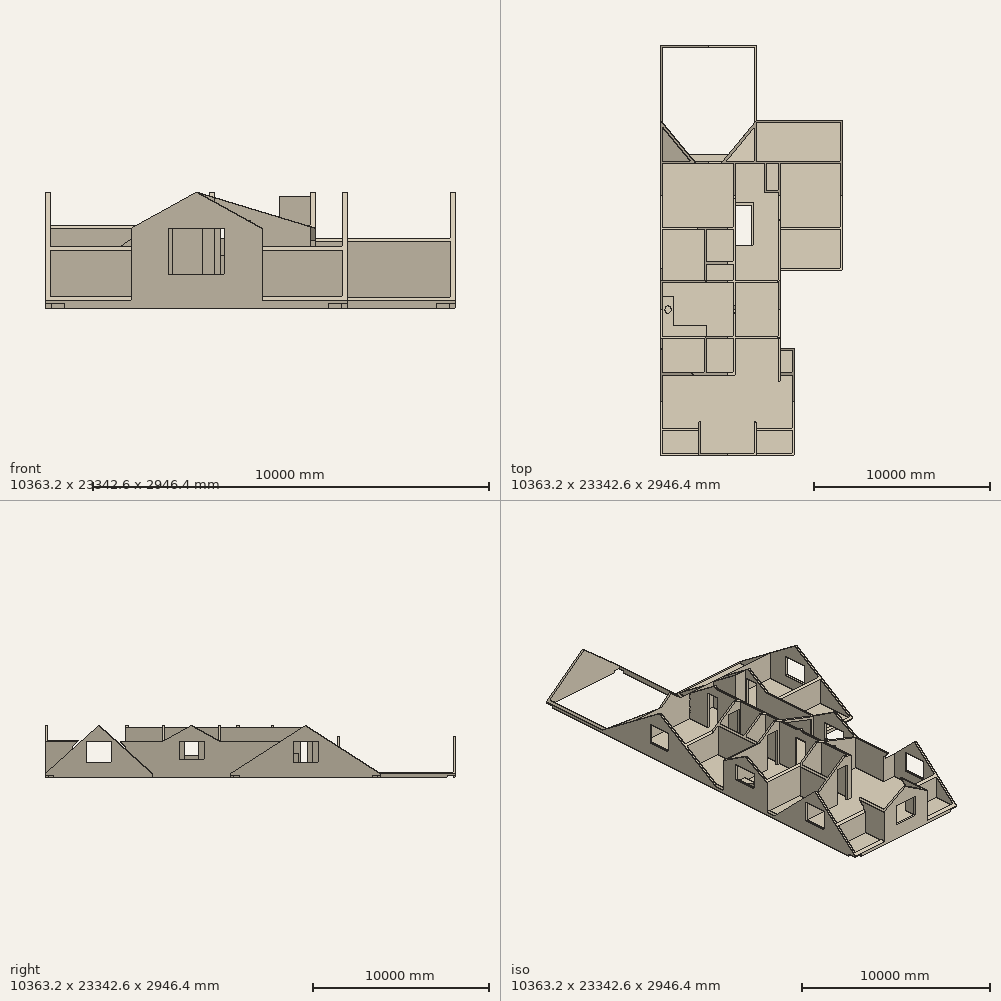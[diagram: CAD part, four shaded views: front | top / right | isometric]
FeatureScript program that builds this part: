
annotation { "Feature Type Name" : "Feature", "Feature Type Description" : "" }
export const myFeature = defineFeature(function(context is Context, id is Id, definition is map)
    precondition{}
    {
        {
            var Q0;
            Q0=qCreatedBy(makeId("Top.planeOp"),FACE);
            cPlane(context, id + "F0", {"entities" : qUnion([Q0]), "cplaneType" : CPlaneType.OFFSET, "offset" : 2946.4 * mm, "width" : 152.4 * mm, "height" : 152.4 * mm});
        }
        {
            var Q0;
            Q0=qCreatedBy(makeId("Top.planeOp"),FACE);
            var sketch = newSketch(context, id + "F1", { "sketchPlane" : qUnion([Q0])});
            skLineSegment(sketch, "E0", {"start": v(0, 0) * mm, "end": v(7645.4, 0) * mm});
            skLineSegment(sketch, "E1", {"start": v(7645.4, 0) * mm, "end": v(7645.4, 6096) * mm});
            skLineSegment(sketch, "E2", {"start": v(7645.4, 6096) * mm, "end": v(6832.6, 6096) * mm});
            skLineSegment(sketch, "E3", {"start": v(6832.6, 6096) * mm, "end": v(6832.6, 10541) * mm});
            skLineSegment(sketch, "E4", {"start": v(6832.6, 10541) * mm, "end": v(10363.2, 10541) * mm});
            skLineSegment(sketch, "E5", {"start": v(10363.2, 10541) * mm, "end": v(10363.2, 19075.4) * mm});
            skLineSegment(sketch, "E6", {"start": v(10363.2, 19075.4) * mm, "end": v(5486.4, 19075.4) * mm});
            skLineSegment(sketch, "E7", {"start": v(5486.4, 19075.4) * mm, "end": v(5486.4, 23342.6) * mm});
            skLineSegment(sketch, "E8", {"start": v(5486.4, 23342.6) * mm, "end": v(0, 23342.6) * mm});
            skLineSegment(sketch, "E9", {"start": v(0, 23342.6) * mm, "end": v(0, 0) * mm});
            skSolve(sketch);
        }
        {
            var Q0;
            Q0=qSketchRegion(id+"F1",true);
            extrude(context, id + "F2", {"entities" : qUnion([Q0]), "depth" : 2946.4 * mm});
        }
        {
            var Q0;
            Q0=makeQuery(id+"F2.opExtrude","SWEPT_FACE",FACE,{"disambiguationData":[OSD([sQuery(id+"F1.wireOp",EDGE,"E5")])]});
            var sketch = newSketch(context, id + "F3", { "sketchPlane" : qUnion([Q0])});
            skLineSegment(sketch, "E10", {"start": v(10541, 203.2) * mm, "end": v(19075.4, 203.2) * mm, "construction": true});
            skLineSegment(sketch, "E11", {"start": v(14808.2, 203.2) * mm, "end": v(14808.2, 2946.4) * mm, "construction": true});
            skLineSegment(sketch, "E12", {"start": v(10541, 203.2) * mm, "end": v(14808.2, 2946.4) * mm});
            skLineSegment(sketch, "E13", {"start": v(10541, 203.2) * mm, "end": v(10541, 2946.4) * mm});
            skLineSegment(sketch, "E14", {"start": v(10541, 2946.4) * mm, "end": v(19075.4, 2946.4) * mm});
            skLineSegment(sketch, "E15", {"start": v(19075.4, 2946.4) * mm, "end": v(19075.4, 203.2) * mm});
            skLineSegment(sketch, "E16", {"start": v(19075.4, 203.2) * mm, "end": v(14808.2, 2946.4) * mm});
            skLineSegment(sketch, "E17", {"start": v(6096, 203.2) * mm, "end": v(0, 203.2) * mm, "construction": true});
            skLineSegment(sketch, "E18", {"start": v(3048, 203.2) * mm, "end": v(3048, 2946.4) * mm, "construction": true});
            skLineSegment(sketch, "E19", {"start": v(3048, 2946.4) * mm, "end": v(0, 203.2) * mm});
            skLineSegment(sketch, "E20", {"start": v(0, 203.2) * mm, "end": v(0, 2946.4) * mm});
            skLineSegment(sketch, "E21", {"start": v(0, 2946.4) * mm, "end": v(6096, 2946.4) * mm});
            skLineSegment(sketch, "E22", {"start": v(6096, 2946.4) * mm, "end": v(6096, 203.2) * mm});
            skLineSegment(sketch, "E23", {"start": v(6096, 203.2) * mm, "end": v(3048, 2946.4) * mm});
            skSolve(sketch);
        }
        {
            var Q0;
            Q0=qSketchRegion(id+"F3",true);
            extrude(context, id + "F4", {"entities" : qUnion([Q0]), "operationType" : NewBodyOperationType.REMOVE, "endBound" : BoundingType.THROUGH_ALL, "oppositeDirection" : true, "depth" : 25.4 * mm});
        }
        {
            var Q0;
            Q0=makeQuery(id+"F2.opExtrude","SWEPT_FACE",FACE,{"disambiguationData":[OSD([sQuery(id+"F1.wireOp",EDGE,"E8")])]});
            var sketch = newSketch(context, id + "F5", { "sketchPlane" : qUnion([Q0])});
            skLineSegment(sketch, "E24", {"start": v(-5486.4, 203.2) * mm, "end": v(0, 203.2) * mm, "construction": true});
            skLineSegment(sketch, "E25", {"start": v(-2743.2, 203.2) * mm, "end": v(-2743.2, 2336.8) * mm, "construction": true});
            skLineSegment(sketch, "E26", {"start": v(-5486.4, 203.2) * mm, "end": v(-2743.2, 2336.8) * mm});
            skLineSegment(sketch, "E27", {"start": v(-2743.2, 2336.8) * mm, "end": v(0, 203.2) * mm});
            skLineSegment(sketch, "E28", {"start": v(-5486.4, 203.2) * mm, "end": v(-5486.4, 2946.4) * mm});
            skLineSegment(sketch, "E29", {"start": v(-5486.4, 2946.4) * mm, "end": v(0, 2946.4) * mm});
            skLineSegment(sketch, "E30", {"start": v(0, 2946.4) * mm, "end": v(0, 203.2) * mm});
            skSolve(sketch);
        }
        {
            var Q0;
            Q0=qSketchRegion(id+"F5",true);
            extrude(context, id + "F6", {"entities" : qUnion([Q0]), "operationType" : NewBodyOperationType.REMOVE, "oppositeDirection" : true, "depth" : 4267.2 * mm});
        }
        {
            var Q0;
            Q0=makeQuery(id+"F4.boolean.opBoolean","COPY",FACE,{"derivedFrom":makeQuery(id+"F4.opExtrude","SWEPT_FACE",FACE,{"disambiguationData":[OSD([sQuery(id+"F3.wireOp",EDGE,"E15")])]})});
            var sketch = newSketch(context, id + "F7", { "sketchPlane" : qUnion([Q0])});
            skLineSegment(sketch, "E31", {"start": v(0, 203.2) * mm, "end": v(2743.2, 2336.8) * mm});
            skLineSegment(sketch, "E32", {"start": v(2743.2, 2336.8) * mm, "end": v(5486.4, 203.2) * mm});
            skLineSegment(sketch, "E33", {"start": v(5486.4, 203.2) * mm, "end": v(0, 203.2) * mm});
            skSolve(sketch);
        }
        {
            var Q0;
            Q0=qSketchRegion(id+"F7",true);
            extrude(context, id + "F8", {"entities" : qUnion([Q0]), "operationType" : NewBodyOperationType.ADD, "endBound" : BoundingType.UP_TO_NEXT, "depth" : 25.4 * mm});
        }
        {
            var Q0;
            Q0=makeQuery(id+"F4.boolean.opBoolean","COPY",FACE,{"derivedFrom":makeQuery(id+"F4.opExtrude","SWEPT_FACE",FACE,{"disambiguationData":[OSD([sQuery(id+"F3.wireOp",EDGE,"E22")])]})});
            var sketch = newSketch(context, id + "F9", { "sketchPlane" : qUnion([Q0])});
            skLineSegment(sketch, "E34", {"start": v(0, 203.2) * mm, "end": v(6832.6, 203.2) * mm, "construction": true});
            skLineSegment(sketch, "E35", {"start": v(3822.7, 203.2) * mm, "end": v(3822.7, 2946.4) * mm, "construction": true});
            skLineSegment(sketch, "E36", {"start": v(6832.6, 203.2) * mm, "end": v(6832.6, 2032) * mm, "construction": true});
            skLineSegment(sketch, "E37", {"start": v(0, 203.2) * mm, "end": v(3822.7, 2946.4) * mm});
            skLineSegment(sketch, "E38", {"start": v(3822.7, 2946.4) * mm, "end": v(6832.6, 2032) * mm});
            skLineSegment(sketch, "E39", {"start": v(6832.6, 2032) * mm, "end": v(6832.6, 2946.4) * mm});
            skLineSegment(sketch, "E40", {"start": v(6832.6, 2946.4) * mm, "end": v(0, 2946.4) * mm});
            skLineSegment(sketch, "E41", {"start": v(0, 2946.4) * mm, "end": v(0, 203.2) * mm});
            skSolve(sketch);
        }
        {
            var Q0;
            Q0=qSketchRegion(id+"F9",true);
            extrude(context, id + "F10", {"entities" : qUnion([Q0]), "operationType" : NewBodyOperationType.REMOVE, "oppositeDirection" : true, "depth" : 4445 * mm});
        }
        {
            var Q0;
            Q0=makeQuery(id+"F4.boolean.opBoolean","COPY",FACE,{"derivedFrom":makeQuery(id+"F4.opExtrude","SWEPT_FACE",FACE,{"disambiguationData":[OSD([sQuery(id+"F3.wireOp",EDGE,"E13")])]})});
            var sketch = newSketch(context, id + "F11", { "sketchPlane" : qUnion([Q0])});
            skLineSegment(sketch, "E42", {"start": v(0, 203.2) * mm, "end": v(-6832.6, 203.2) * mm});
            skLineSegment(sketch, "E43", {"start": v(-6832.6, 203.2) * mm, "end": v(-6832.6, 2032) * mm});
            skLineSegment(sketch, "E44", {"start": v(-6832.6, 2032) * mm, "end": v(-3822.7, 2946.4) * mm});
            skLineSegment(sketch, "E45", {"start": v(-3822.7, 2946.4) * mm, "end": v(0, 203.2) * mm});
            skSolve(sketch);
        }
        {
            var Q0;
            Q0=qSketchRegion(id+"F11",true);
            extrude(context, id + "F12", {"entities" : qUnion([Q0]), "operationType" : NewBodyOperationType.ADD, "endBound" : BoundingType.UP_TO_NEXT, "depth" : 25.4 * mm});
        }
        {
            var Q0;
            Q0=makeQuery(id+"F4.boolean.opBoolean","COPY",FACE,{"derivedFrom":makeQuery(id+"F4.opExtrude","SWEPT_FACE",FACE,{"disambiguationData":[OSD([sQuery(id+"F3.wireOp",EDGE,"E22")])]})});
            var sketch = newSketch(context, id + "F13", { "sketchPlane" : qUnion([Q0])});
            skLineSegment(sketch, "E46", {"start": v(0, 203.2) * mm, "end": v(3822.7, 2946.4) * mm});
            skLineSegment(sketch, "E47", {"start": v(3822.7, 2946.4) * mm, "end": v(6832.6, 2032) * mm});
            skLineSegment(sketch, "E48", {"start": v(6832.6, 2032) * mm, "end": v(6832.6, 203.2) * mm});
            skLineSegment(sketch, "E49", {"start": v(6832.6, 203.2) * mm, "end": v(0, 203.2) * mm});
            skSolve(sketch);
        }
        {
            var Q0;
            Q0=qSketchRegion(id+"F13",true);
            extrude(context, id + "F14", {"entities" : qUnion([Q0]), "operationType" : NewBodyOperationType.ADD, "endBound" : BoundingType.UP_TO_NEXT, "depth" : 25.4 * mm});
        }
        {
            var Q0;
            Q0=makeQuery(id+"F14.boolean.opBoolean","MERGE",FACE,{"derivedFrom":[makeQuery(id+"F12.boolean.opBoolean","MERGE",FACE,{"derivedFrom":[makeQuery(id+"F2.opExtrude","SWEPT_FACE",FACE,{"disambiguationData":[OSD([sQuery(id+"F1.wireOp",EDGE,"E3")])]}),makeQuery(id+"F12.opExtrude","SWEPT_FACE",FACE,{"disambiguationData":[OSD([sQuery(id+"F11.wireOp",EDGE,"E43")])]})]}),makeQuery(id+"F14.opExtrude","SWEPT_FACE",FACE,{"disambiguationData":[OSD([sQuery(id+"F13.wireOp",EDGE,"E48")])]})]});
            var sketch = newSketch(context, id + "F15", { "sketchPlane" : qUnion([Q0])});
            skLineSegment(sketch, "E50", {"start": v(6667.5, 203.2) * mm, "end": v(9969.5, 203.2) * mm, "construction": true});
            skLineSegment(sketch, "E51", {"start": v(8318.5, 203.2) * mm, "end": v(8318.5, 2946.4) * mm, "construction": true});
            skLineSegment(sketch, "E52", {"start": v(6667.5, 203.2) * mm, "end": v(6667.5, 2032) * mm, "construction": true});
            skLineSegment(sketch, "E53", {"start": v(6667.5, 2032) * mm, "end": v(8318.5, 2946.4) * mm});
            skLineSegment(sketch, "E54.MirrorCS", {"start": v(9969.5, 2032) * mm, "end": v(8318.5, 2946.4) * mm});
            skLineSegment(sketch, "E55", {"start": v(6667.5, 2032) * mm, "end": v(9969.5, 2032) * mm});
            skSolve(sketch);
        }
        {
            var Q0;
            Q0=qSketchRegion(id+"F15",true);
            extrude(context, id + "F16", {"entities" : qUnion([Q0]), "operationType" : NewBodyOperationType.ADD, "endBound" : BoundingType.UP_TO_NEXT, "oppositeDirection" : true, "depth" : 25.4 * mm});
        }
        {
            var Q0;
            Q0=makeQuery(id+"F2.opExtrude","SWEPT_FACE",FACE,{"disambiguationData":[OSD([sQuery(id+"F1.wireOp",EDGE,"E9")])]});
            var sketch = newSketch(context, id + "F17", { "sketchPlane" : qUnion([Q0])});
            skLineSegment(sketch, "E56", {"start": v(-9969.5, 203.2) * mm, "end": v(-6667.5, 203.2) * mm});
            skLineSegment(sketch, "E57", {"start": v(-8318.5, 203.2) * mm, "end": v(-8318.5, 2946.4) * mm, "construction": true});
            skLineSegment(sketch, "E58", {"start": v(-9969.5, 203.2) * mm, "end": v(-9969.5, 2032) * mm});
            skLineSegment(sketch, "E59", {"start": v(-9969.5, 2032) * mm, "end": v(-8318.5, 2946.4) * mm});
            skLineSegment(sketch, "E60.MirrorCS", {"start": v(-6667.5, 203.2) * mm, "end": v(-6667.5, 2032) * mm});
            skLineSegment(sketch, "E61.MirrorCS", {"start": v(-6667.5, 2032) * mm, "end": v(-8318.5, 2946.4) * mm});
            skSolve(sketch);
        }
        {
            var Q0;
            Q0=qSketchRegion(id+"F17",true);
            extrude(context, id + "F18", {"entities" : qUnion([Q0]), "operationType" : NewBodyOperationType.ADD, "endBound" : BoundingType.UP_TO_NEXT, "oppositeDirection" : true, "depth" : 25.4 * mm});
        }
        {
            var Q0;
            Q0=makeQuery(id+"F2.opExtrude","SWEPT_FACE",FACE,{"disambiguationData":[OSD([sQuery(id+"F1.wireOp",EDGE,"E0")])]});
            var sketch = newSketch(context, id + "F19", { "sketchPlane" : qUnion([Q0])});
            skLineSegment(sketch, "E62", {"start": v(2171.7, 203.2) * mm, "end": v(5473.7, 203.2) * mm});
            skLineSegment(sketch, "E63", {"start": v(3822.7, 203.2) * mm, "end": v(3822.7, 2946.4) * mm, "construction": true});
            skLineSegment(sketch, "E64", {"start": v(2171.7, 203.2) * mm, "end": v(2171.7, 2032) * mm});
            skLineSegment(sketch, "E65", {"start": v(2171.7, 2032) * mm, "end": v(3822.7, 2946.4) * mm});
            skLineSegment(sketch, "E66.MirrorCS", {"start": v(5473.7, 203.2) * mm, "end": v(5473.7, 2032) * mm});
            skLineSegment(sketch, "E67.MirrorCS", {"start": v(5473.7, 2032) * mm, "end": v(3822.7, 2946.4) * mm});
            skSolve(sketch);
        }
        {
            var Q0;
            Q0=qSketchRegion(id+"F19",true);
            extrude(context, id + "F20", {"entities" : qUnion([Q0]), "operationType" : NewBodyOperationType.ADD, "endBound" : BoundingType.UP_TO_NEXT, "oppositeDirection" : true, "depth" : 25.4 * mm});
        }
        {
            var Q0;
            Q0=qCreatedBy(id+"F0.planeOp",FACE);
            var sketch = newSketch(context, id + "F21", { "sketchPlane" : qUnion([Q0])});
            skLineSegment(sketch, "E68.bottom", {"start": v(127, 23215.6) * mm, "end": v(5359.4, 23215.6) * mm});
            skLineSegment(sketch, "E68.top", {"start": v(127, 16764) * mm, "end": v(5359.4, 16764) * mm});
            skLineSegment(sketch, "E68.left", {"start": v(127, 23215.6) * mm, "end": v(127, 16764) * mm});
            skLineSegment(sketch, "E68.right", {"start": v(5359.4, 23215.6) * mm, "end": v(5359.4, 16764) * mm});
            skLineSegment(sketch, "E69.bottom", {"start": v(5486.4, 18948.4) * mm, "end": v(10236.2, 18948.4) * mm});
            skLineSegment(sketch, "E69.top", {"start": v(5486.4, 16764) * mm, "end": v(10236.2, 16764) * mm});
            skLineSegment(sketch, "E69.left", {"start": v(5486.4, 18948.4) * mm, "end": v(5486.4, 16764) * mm});
            skLineSegment(sketch, "E69.right", {"start": v(10236.2, 18948.4) * mm, "end": v(10236.2, 16764) * mm});
            skLineSegment(sketch, "E70.bottom", {"start": v(6832.6, 16637) * mm, "end": v(10236.2, 16637) * mm});
            skLineSegment(sketch, "E70.top", {"start": v(6832.6, 12979.4) * mm, "end": v(10236.2, 12979.4) * mm});
            skLineSegment(sketch, "E70.left", {"start": v(6832.6, 16637) * mm, "end": v(6832.6, 12979.4) * mm});
            skLineSegment(sketch, "E70.right", {"start": v(10236.2, 16637) * mm, "end": v(10236.2, 12979.4) * mm});
            skLineSegment(sketch, "E71.bottom", {"start": v(6832.6, 12852.4) * mm, "end": v(10236.2, 12852.4) * mm});
            skLineSegment(sketch, "E71.top", {"start": v(6832.6, 10668) * mm, "end": v(10236.2, 10668) * mm});
            skLineSegment(sketch, "E71.left", {"start": v(6832.6, 12852.4) * mm, "end": v(6832.6, 10668) * mm});
            skLineSegment(sketch, "E71.right", {"start": v(10236.2, 12852.4) * mm, "end": v(10236.2, 10668) * mm});
            skLineSegment(sketch, "E72.bottom", {"start": v(6032.5, 16637) * mm, "end": v(6705.6, 16637) * mm});
            skLineSegment(sketch, "E72.top", {"start": v(6032.5, 15113) * mm, "end": v(6705.6, 15113) * mm});
            skLineSegment(sketch, "E72.left", {"start": v(6032.5, 16637) * mm, "end": v(6032.5, 15113) * mm});
            skLineSegment(sketch, "E72.right", {"start": v(6705.6, 16637) * mm, "end": v(6705.6, 15113) * mm});
            skLineSegment(sketch, "E73.bottom", {"start": v(127, 16637) * mm, "end": v(4140.2, 16637) * mm});
            skLineSegment(sketch, "E73.top", {"start": v(127, 12979.4) * mm, "end": v(4140.2, 12979.4) * mm});
            skLineSegment(sketch, "E73.left", {"start": v(127, 16637) * mm, "end": v(127, 12979.4) * mm});
            skLineSegment(sketch, "E73.right", {"start": v(4140.2, 16637) * mm, "end": v(4140.2, 12979.4) * mm});
            skLineSegment(sketch, "E74.bottom", {"start": v(127, 12852.4) * mm, "end": v(2489.2, 12852.4) * mm});
            skLineSegment(sketch, "E74.top", {"start": v(127, 9969.5) * mm, "end": v(2489.2, 9969.5) * mm});
            skLineSegment(sketch, "E74.left", {"start": v(127, 12852.4) * mm, "end": v(127, 9969.5) * mm});
            skLineSegment(sketch, "E74.right", {"start": v(2489.2, 12852.4) * mm, "end": v(2489.2, 9969.5) * mm});
            skLineSegment(sketch, "E75.bottom", {"start": v(2616.2, 12852.4) * mm, "end": v(4140.2, 12852.4) * mm});
            skLineSegment(sketch, "E75.top", {"start": v(2616.2, 11023.6) * mm, "end": v(4140.2, 11023.6) * mm});
            skLineSegment(sketch, "E75.left", {"start": v(2616.2, 12852.4) * mm, "end": v(2616.2, 11023.6) * mm});
            skLineSegment(sketch, "E75.right", {"start": v(4140.2, 12852.4) * mm, "end": v(4140.2, 11023.6) * mm});
            skLineSegment(sketch, "E76.bottom", {"start": v(2616.2, 10896.6) * mm, "end": v(4140.2, 10896.6) * mm});
            skLineSegment(sketch, "E76.top", {"start": v(2616.2, 9969.5) * mm, "end": v(4140.2, 9969.5) * mm});
            skLineSegment(sketch, "E76.left", {"start": v(2616.2, 10896.6) * mm, "end": v(2616.2, 9969.5) * mm});
            skLineSegment(sketch, "E76.right", {"start": v(4140.2, 10896.6) * mm, "end": v(4140.2, 9969.5) * mm});
            skLineSegment(sketch, "E77.bottom", {"start": v(127, 9842.5) * mm, "end": v(4140.2, 9842.5) * mm});
            skLineSegment(sketch, "E77.top", {"start": v(127, 6794.5) * mm, "end": v(4140.2, 6794.5) * mm});
            skLineSegment(sketch, "E77.left", {"start": v(127, 9842.5) * mm, "end": v(127, 6794.5) * mm});
            skLineSegment(sketch, "E77.right", {"start": v(4140.2, 9842.5) * mm, "end": v(4140.2, 6794.5) * mm});
            skLineSegment(sketch, "E78.bottom", {"start": v(127, 6667.5) * mm, "end": v(2489.2, 6667.5) * mm});
            skLineSegment(sketch, "E78.top", {"start": v(127, 4699) * mm, "end": v(2489.2, 4699) * mm});
            skLineSegment(sketch, "E78.left", {"start": v(127, 6667.5) * mm, "end": v(127, 4699) * mm});
            skLineSegment(sketch, "E78.right", {"start": v(2489.2, 6667.5) * mm, "end": v(2489.2, 4699) * mm});
            skLineSegment(sketch, "E79.bottom", {"start": v(2616.2, 6667.5) * mm, "end": v(4140.2, 6667.5) * mm});
            skLineSegment(sketch, "E79.top", {"start": v(2616.2, 4699) * mm, "end": v(4140.2, 4699) * mm});
            skLineSegment(sketch, "E79.left", {"start": v(2616.2, 6667.5) * mm, "end": v(2616.2, 4699) * mm});
            skLineSegment(sketch, "E79.right", {"start": v(4140.2, 6667.5) * mm, "end": v(4140.2, 4699) * mm});
            skLineSegment(sketch, "E80.bottom", {"start": v(127, 1397) * mm, "end": v(2171.7, 1397) * mm});
            skLineSegment(sketch, "E80.top", {"start": v(127, 127) * mm, "end": v(2171.7, 127) * mm});
            skLineSegment(sketch, "E80.left", {"start": v(127, 1397) * mm, "end": v(127, 127) * mm});
            skLineSegment(sketch, "E80.right", {"start": v(2171.7, 1397) * mm, "end": v(2171.7, 127) * mm});
            skLineSegment(sketch, "E81.bottom", {"start": v(5473.7, 1397) * mm, "end": v(7518.4, 1397) * mm});
            skLineSegment(sketch, "E81.top", {"start": v(5473.7, 127) * mm, "end": v(7518.4, 127) * mm});
            skLineSegment(sketch, "E81.left", {"start": v(5473.7, 1397) * mm, "end": v(5473.7, 127) * mm});
            skLineSegment(sketch, "E81.right", {"start": v(7518.4, 1397) * mm, "end": v(7518.4, 127) * mm});
            skLineSegment(sketch, "E82.bottom", {"start": v(6832.6, 5969) * mm, "end": v(7518.4, 5969) * mm});
            skLineSegment(sketch, "E82.top", {"start": v(6832.6, 4699) * mm, "end": v(7518.4, 4699) * mm});
            skLineSegment(sketch, "E82.left", {"start": v(6832.6, 5969) * mm, "end": v(6832.6, 4699) * mm});
            skLineSegment(sketch, "E82.right", {"start": v(7518.4, 5969) * mm, "end": v(7518.4, 4699) * mm});
            skLineSegment(sketch, "E83", {"start": v(127, 4572) * mm, "end": v(127, 1524) * mm});
            skLineSegment(sketch, "E84", {"start": v(127, 1524) * mm, "end": v(2298.7, 1524) * mm});
            skLineSegment(sketch, "E85", {"start": v(7518.4, 1524) * mm, "end": v(7518.4, 4572) * mm});
            skLineSegment(sketch, "E86", {"start": v(7518.4, 4572) * mm, "end": v(6705.6, 4572) * mm});
            skLineSegment(sketch, "E87", {"start": v(6705.6, 4572) * mm, "end": v(6705.6, 6667.5) * mm});
            skLineSegment(sketch, "E88", {"start": v(6705.6, 6667.5) * mm, "end": v(4267.2, 6667.5) * mm});
            skLineSegment(sketch, "E89", {"start": v(4267.2, 6667.5) * mm, "end": v(4267.2, 4572) * mm});
            skLineSegment(sketch, "E90", {"start": v(4267.2, 4572) * mm, "end": v(127, 4572) * mm});
            skLineSegment(sketch, "E91", {"start": v(4267.2, 16637) * mm, "end": v(4267.2, 9969.5) * mm});
            skLineSegment(sketch, "E92", {"start": v(4267.2, 6794.5) * mm, "end": v(6705.6, 6794.5) * mm});
            skLineSegment(sketch, "E93", {"start": v(6705.6, 6794.5) * mm, "end": v(6705.6, 9842.5) * mm});
            skLineSegment(sketch, "E94", {"start": v(6705.6, 14986) * mm, "end": v(5905.5, 14986) * mm});
            skLineSegment(sketch, "E95", {"start": v(5905.5, 14986) * mm, "end": v(5905.5, 16637) * mm});
            skLineSegment(sketch, "E96", {"start": v(5905.5, 16637) * mm, "end": v(4267.2, 16637) * mm});
            skLineSegment(sketch, "E97", {"start": v(2298.7, 1524) * mm, "end": v(2298.7, 127) * mm});
            skLineSegment(sketch, "E98", {"start": v(2298.7, 127) * mm, "end": v(5346.7, 127) * mm});
            skLineSegment(sketch, "E99", {"start": v(5346.7, 127) * mm, "end": v(5346.7, 1524) * mm});
            skLineSegment(sketch, "E100.trimOffspring", {"start": v(5346.7, 1524) * mm, "end": v(7518.4, 1524) * mm});
            skLineSegment(sketch, "E101", {"start": v(4267.2, 9842.5) * mm, "end": v(6705.6, 9842.5) * mm});
            skLineSegment(sketch, "E102", {"start": v(6705.6, 9969.5) * mm, "end": v(4267.2, 9969.5) * mm});
            skLineSegment(sketch, "E103.trimOffspring", {"start": v(4267.2, 9842.5) * mm, "end": v(4267.2, 6794.5) * mm});
            skLineSegment(sketch, "E104.trimOffspring", {"start": v(6705.6, 9969.5) * mm, "end": v(6705.6, 14986) * mm});
            skSolve(sketch);
        }
        {
            var Q0;
            Q0=qSketchRegion(id+"F21",true);
            extrude(context, id + "F22", {"entities" : qUnion([Q0]), "operationType" : NewBodyOperationType.REMOVE, "oppositeDirection" : true, "depth" : 2743.2 * mm});
        }
        {
            var Q0;
            Q0=makeQuery(id+"F22.boolean.opBoolean","COPY",FACE,{"derivedFrom":makeQuery(id+"F22.opExtrude","SWEPT_FACE",FACE,{"disambiguationData":[OSD([sQuery(id+"F21.wireOp",EDGE,"E100.trimOffspring")])]})});
            var sketch = newSketch(context, id + "F23", { "sketchPlane" : qUnion([Q0])});
            skLineSegment(sketch, "E105", {"start": v(-5346.7, 1727.2) * mm, "end": v(-5473.7, 1727.2) * mm});
            skLineSegment(sketch, "E106", {"start": v(-5473.7, 1727.2) * mm, "end": v(-5473.7, 2032) * mm});
            skLineSegment(sketch, "E107", {"start": v(-5473.7, 2032) * mm, "end": v(-5346.7, 2102.34) * mm});
            skLineSegment(sketch, "E108", {"start": v(-5346.7, 2102.34) * mm, "end": v(-5346.7, 1727.2) * mm});
            skLineSegment(sketch, "E109", {"start": v(-2298.7, 1727.2) * mm, "end": v(-2171.7, 1727.2) * mm});
            skLineSegment(sketch, "E110", {"start": v(-2171.7, 1727.2) * mm, "end": v(-2171.7, 2032) * mm});
            skLineSegment(sketch, "E111", {"start": v(-2171.7, 2032) * mm, "end": v(-2298.7, 2102.34) * mm});
            skLineSegment(sketch, "E112", {"start": v(-2298.7, 2102.34) * mm, "end": v(-2298.7, 1727.2) * mm});
            skSolve(sketch);
        }
        {
            var Q0;
            Q0=qSketchRegion(id+"F23",true);
            extrude(context, id + "F24", {"entities" : qUnion([Q0]), "operationType" : NewBodyOperationType.ADD, "depth" : 609.6 * mm});
        }
        {
            var Q0;
            Q0=makeQuery(id+"F24.boolean.opBoolean","MERGE",FACE,{"derivedFrom":[makeQuery(id+"F22.boolean.opBoolean","MERGE",FACE,{"derivedFrom":[makeQuery(id+"F20.opExtrude","SWEPT_FACE",FACE,{"disambiguationData":[OSD([sQuery(id+"F19.wireOp",EDGE,"E66.MirrorCS")])]}),makeQuery(id+"F22.opExtrude","SWEPT_FACE",FACE,{"disambiguationData":[OSD([sQuery(id+"F21.wireOp",EDGE,"E81.left")])]})]}),makeQuery(id+"F24.opExtrude","SWEPT_FACE",FACE,{"disambiguationData":[OSD([sQuery(id+"F23.wireOp",EDGE,"E106")])]})]});
            var sketch = newSketch(context, id + "F25", { "sketchPlane" : qUnion([Q0])});
            skLineSegment(sketch, "E113", {"start": v(1524, 1727.2) * mm, "end": v(1940.82, 2102.34) * mm});
            skLineSegment(sketch, "E114", {"start": v(1940.82, 2102.34) * mm, "end": v(2133.6, 2102.34) * mm});
            skLineSegment(sketch, "E115", {"start": v(2133.6, 2102.34) * mm, "end": v(2133.6, 1727.2) * mm});
            skLineSegment(sketch, "E116", {"start": v(2133.6, 1727.2) * mm, "end": v(1524, 1727.2) * mm});
            skSolve(sketch);
        }
        {
            var Q0;
            Q0=qSketchRegion(id+"F25",true);
            var Q1;
            Q1=makeQuery(id+"F24.boolean.opBoolean","MERGE",FACE,{"derivedFrom":[makeQuery(id+"F22.boolean.opBoolean","MERGE",FACE,{"derivedFrom":[makeQuery(id+"F20.opExtrude","SWEPT_FACE",FACE,{"disambiguationData":[OSD([sQuery(id+"F19.wireOp",EDGE,"E64")])]}),makeQuery(id+"F22.opExtrude","SWEPT_FACE",FACE,{"disambiguationData":[OSD([sQuery(id+"F21.wireOp",EDGE,"E80.right")])]})]}),makeQuery(id+"F24.opExtrude","SWEPT_FACE",FACE,{"disambiguationData":[OSD([sQuery(id+"F23.wireOp",EDGE,"E110")])]})]});
            extrude(context, id + "F26", {"entities" : qUnion([Q0]), "operationType" : NewBodyOperationType.REMOVE, "endBound" : BoundingType.UP_TO_SURFACE, "oppositeDirection" : true, "endBoundEntityFace" : qUnion([Q1]), "depth" : 25.4 * mm});
        }
        {
            var Q0;
            Q0=makeQuery(id+"F22.boolean.opBoolean","COPY",FACE,{"derivedFrom":makeQuery(id+"F22.opExtrude","SWEPT_FACE",FACE,{"disambiguationData":[OSD([sQuery(id+"F21.wireOp",EDGE,"E86")])]})});
            var sketch = newSketch(context, id + "F27", { "sketchPlane" : qUnion([Q0])});
            skLineSegment(sketch, "E117", {"start": v(6705.6, 1727.2) * mm, "end": v(6832.6, 1727.2) * mm});
            skLineSegment(sketch, "E118", {"start": v(6832.6, 1727.2) * mm, "end": v(6832.6, 2032) * mm});
            skLineSegment(sketch, "E119", {"start": v(6832.6, 2032) * mm, "end": v(6705.6, 2070.58) * mm});
            skLineSegment(sketch, "E120", {"start": v(6705.6, 2070.58) * mm, "end": v(6705.6, 1727.2) * mm});
            skSolve(sketch);
        }
        {
            var Q0;
            Q0=qSketchRegion(id+"F27",true);
            extrude(context, id + "F28", {"entities" : qUnion([Q0]), "operationType" : NewBodyOperationType.ADD, "depth" : 609.6 * mm});
        }
        {
            var Q0;
            Q0=makeQuery(id+"F28.boolean.opBoolean","MERGE",FACE,{"derivedFrom":[makeQuery(id+"F22.boolean.opBoolean","MERGE",FACE,{"derivedFrom":[makeQuery(id+"F16.boolean.opBoolean","MERGE",FACE,{"derivedFrom":[makeQuery(id+"F14.boolean.opBoolean","MERGE",FACE,{"derivedFrom":[makeQuery(id+"F12.boolean.opBoolean","MERGE",FACE,{"derivedFrom":[makeQuery(id+"F2.opExtrude","SWEPT_FACE",FACE,{"disambiguationData":[OSD([sQuery(id+"F1.wireOp",EDGE,"E3")])]}),makeQuery(id+"F12.opExtrude","SWEPT_FACE",FACE,{"disambiguationData":[OSD([sQuery(id+"F11.wireOp",EDGE,"E43")])]})]}),makeQuery(id+"F14.opExtrude","SWEPT_FACE",FACE,{"disambiguationData":[OSD([sQuery(id+"F13.wireOp",EDGE,"E48")])]})]}),makeQuery(id+"F16.opExtrude","CAP_FACE",FACE,{"disambiguationData":[OSD([sQuery(id+"F15.wireOp",EDGE,"E53"),sQuery(id+"F15.wireOp",EDGE,"E54.MirrorCS"),sQuery(id+"F15.wireOp",EDGE,"E55")])],"isStart":true})]}),makeQuery(id+"F22.opExtrude","SWEPT_FACE",FACE,{"disambiguationData":[OSD([sQuery(id+"F21.wireOp",EDGE,"E70.left")])]}),makeQuery(id+"F22.opExtrude","SWEPT_FACE",FACE,{"disambiguationData":[OSD([sQuery(id+"F21.wireOp",EDGE,"E71.left")])]}),makeQuery(id+"F22.opExtrude","SWEPT_FACE",FACE,{"disambiguationData":[OSD([sQuery(id+"F21.wireOp",EDGE,"E82.left")])]})]}),makeQuery(id+"F28.opExtrude","SWEPT_FACE",FACE,{"disambiguationData":[OSD([sQuery(id+"F27.wireOp",EDGE,"E118")])]})]});
            var sketch = newSketch(context, id + "F29", { "sketchPlane" : qUnion([Q0])});
            skLineSegment(sketch, "E121", {"start": v(4572, 1727.2) * mm, "end": v(4190.46, 2070.58) * mm});
            skLineSegment(sketch, "E122", {"start": v(4190.46, 2070.58) * mm, "end": v(3962.4, 2070.58) * mm});
            skLineSegment(sketch, "E123", {"start": v(3962.4, 2070.58) * mm, "end": v(3962.4, 1727.2) * mm});
            skLineSegment(sketch, "E124", {"start": v(3962.4, 1727.2) * mm, "end": v(4572, 1727.2) * mm});
            skSolve(sketch);
        }
        {
            var Q0;
            Q0=qSketchRegion(id+"F29",true);
            extrude(context, id + "F30", {"entities" : qUnion([Q0]), "operationType" : NewBodyOperationType.REMOVE, "endBound" : BoundingType.UP_TO_NEXT, "oppositeDirection" : true, "depth" : 25.4 * mm});
        }
        {
            var Q0;
            Q0=makeQuery(id+"F22.boolean.opBoolean","COPY",FACE,{"derivedFrom":makeQuery(id+"F22.opExtrude","CAP_FACE",FACE,{"disambiguationData":[OSD([sQuery(id+"F21.wireOp",EDGE,"E68.bottom"),sQuery(id+"F21.wireOp",EDGE,"E68.top"),sQuery(id+"F21.wireOp",EDGE,"E68.left"),sQuery(id+"F21.wireOp",EDGE,"E68.right")])],"isStart":false})});
            var sketch = newSketch(context, id + "F31", { "sketchPlane" : qUnion([Q0])});
            skLineSegment(sketch, "E125.bottom", {"start": v(127, 23215.6) * mm, "end": v(5359.4, 23215.6) * mm});
            skLineSegment(sketch, "E125.top", {"start": v(127, 17119.6) * mm, "end": v(5359.4, 17119.6) * mm});
            skLineSegment(sketch, "E125.left", {"start": v(127, 23215.6) * mm, "end": v(127, 17119.6) * mm});
            skLineSegment(sketch, "E125.right", {"start": v(5359.4, 23215.6) * mm, "end": v(5359.4, 17119.6) * mm});
            skSolve(sketch);
        }
        {
            var Q0;
            Q0=qSketchRegion(id+"F31",true);
            extrude(context, id + "F32", {"entities" : qUnion([Q0]), "operationType" : NewBodyOperationType.REMOVE, "endBound" : BoundingType.UP_TO_NEXT, "oppositeDirection" : true, "depth" : 25.4 * mm});
        }
        {
            var Q0;
            Q0=makeQuery(id+"F22.boolean.opBoolean","COPY",FACE,{"derivedFrom":makeQuery(id+"F22.opExtrude","CAP_FACE",FACE,{"disambiguationData":[OSD([sQuery(id+"F21.wireOp",EDGE,"E91"),sQuery(id+"F21.wireOp",EDGE,"E94"),sQuery(id+"F21.wireOp",EDGE,"E95"),sQuery(id+"F21.wireOp",EDGE,"E96"),sQuery(id+"F21.wireOp",EDGE,"E102"),sQuery(id+"F21.wireOp",EDGE,"E104.trimOffspring")])],"isStart":false})});
            var sketch = newSketch(context, id + "F33", { "sketchPlane" : qUnion([Q0])});
            skLineSegment(sketch, "E126.bottom", {"start": v(4267.2, 11963.4) * mm, "end": v(5181.6, 11963.4) * mm});
            skLineSegment(sketch, "E126.top", {"start": v(4267.2, 14249.4) * mm, "end": v(5181.6, 14249.4) * mm});
            skLineSegment(sketch, "E126.left", {"start": v(4267.2, 11963.4) * mm, "end": v(4267.2, 14249.4) * mm});
            skLineSegment(sketch, "E126.right", {"start": v(5181.6, 11963.4) * mm, "end": v(5181.6, 14249.4) * mm});
            skSolve(sketch);
        }
        {
            var Q0;
            Q0=qSketchRegion(id+"F33",true);
            extrude(context, id + "F34", {"entities" : qUnion([Q0]), "operationType" : NewBodyOperationType.REMOVE, "endBound" : BoundingType.UP_TO_NEXT, "oppositeDirection" : true, "depth" : 25.4 * mm});
        }
        {
            var Q0;
            Q0=makeQuery(id+"F22.boolean.opBoolean","COPY",FACE,{"derivedFrom":makeQuery(id+"F22.opExtrude","CAP_FACE",FACE,{"disambiguationData":[OSD([sQuery(id+"F21.wireOp",EDGE,"E91"),sQuery(id+"F21.wireOp",EDGE,"E94"),sQuery(id+"F21.wireOp",EDGE,"E95"),sQuery(id+"F21.wireOp",EDGE,"E96"),sQuery(id+"F21.wireOp",EDGE,"E102"),sQuery(id+"F21.wireOp",EDGE,"E104.trimOffspring")])],"isStart":false})});
            var sketch = newSketch(context, id + "F35", { "sketchPlane" : qUnion([Q0])});
            skLineSegment(sketch, "E127", {"start": v(4267.2, 14249.4) * mm, "end": v(5181.6, 14249.4) * mm});
            skLineSegment(sketch, "E128", {"start": v(5181.6, 14249.4) * mm, "end": v(5181.6, 11963.4) * mm});
            skLineSegment(sketch, "E129", {"start": v(5181.6, 11963.4) * mm, "end": v(5308.6, 11963.4) * mm});
            skLineSegment(sketch, "E130", {"start": v(5308.6, 11963.4) * mm, "end": v(5308.6, 14376.4) * mm});
            skLineSegment(sketch, "E131", {"start": v(5308.6, 14376.4) * mm, "end": v(4267.2, 14376.4) * mm});
            skLineSegment(sketch, "E132", {"start": v(4267.2, 14376.4) * mm, "end": v(4267.2, 14249.4) * mm});
            skSolve(sketch);
        }
        {
            var Q0;
            Q0=qSketchRegion(id+"F35",true);
            extrude(context, id + "F36", {"entities" : qUnion([Q0]), "operationType" : NewBodyOperationType.ADD, "depth" : 1143 * mm});
        }
        {
            var Q0;
            Q0=makeQuery(id+"F34.boolean.opBoolean","MERGE",FACE,{"derivedFrom":[makeQuery(id+"F22.boolean.opBoolean","COPY",FACE,{"derivedFrom":makeQuery(id+"F22.opExtrude","SWEPT_FACE",FACE,{"disambiguationData":[OSD([sQuery(id+"F21.wireOp",EDGE,"E91")])]})}),makeQuery(id+"F34.opExtrude","SWEPT_FACE",FACE,{"disambiguationData":[OSD([sQuery(id+"F33.wireOp",EDGE,"E126.left")])]})]});
            var sketch = newSketch(context, id + "F37", { "sketchPlane" : qUnion([Q0])});
            skLineSegment(sketch, "E133", {"start": v(14249.4, 0) * mm, "end": v(14503.4, 0) * mm});
            skLineSegment(sketch, "E134", {"start": v(14503.4, 0) * mm, "end": v(14249.4, 203.2) * mm});
            skLineSegment(sketch, "E135", {"start": v(14249.4, 203.2) * mm, "end": v(14249.4, 0) * mm});
            skSolve(sketch);
        }
        {
            var Q0;
            Q0=qSketchRegion(id+"F37",true);
            extrude(context, id + "F38", {"entities" : qUnion([Q0]), "operationType" : NewBodyOperationType.REMOVE, "depth" : 914.4 * mm});
        }
        {
            var Q0;
            Q0=makeQuery(id+"F22.boolean.opBoolean","SPLIT",FACE,{"disambiguationData":[TD([makeQuery(id+"F2.opExtrude","SWEPT_FACE",FACE,{"disambiguationData":[OSD([sQuery(id+"F1.wireOp",EDGE,"E6")])]})])],"derivedFrom":makeQuery(id+"F8.boolean.opBoolean","MERGE",FACE,{"derivedFrom":[makeQuery(id+"F6.boolean.opBoolean","COPY",FACE,{"derivedFrom":makeQuery(id+"F6.opExtrude","SWEPT_FACE",FACE,{"disambiguationData":[OSD([sQuery(id+"F5.wireOp",EDGE,"E26")])]})}),makeQuery(id+"F8.opExtrude","SWEPT_FACE",FACE,{"disambiguationData":[OSD([sQuery(id+"F7.wireOp",EDGE,"E32")])]})]})});
            var sketch = newSketch(context, id + "F39", { "sketchPlane" : qUnion([Q0])});
            skLineSegment(sketch, "E136", {"start": v(4045.06, 18921.75) * mm, "end": v(1785.68, 16764) * mm});
            skLineSegment(sketch, "E137", {"start": v(1785.68, 16764) * mm, "end": v(4045.06, 16764) * mm});
            skLineSegment(sketch, "E138", {"start": v(4045.06, 16764) * mm, "end": v(4045.06, 18921.75) * mm});
            skSolve(sketch);
        }
        {
            var Q0;
            Q0=qSketchRegion(id+"F39",true);
            extrude(context, id + "F40", {"entities" : qUnion([Q0]), "operationType" : NewBodyOperationType.ADD, "depth" : 127 * mm});
        }
        {
            var Q0;
            Q0=makeQuery(id+"F22.boolean.opBoolean","SPLIT",FACE,{"disambiguationData":[TD([makeQuery(id+"F2.opExtrude","SWEPT_FACE",FACE,{"disambiguationData":[OSD([sQuery(id+"F1.wireOp",EDGE,"E8")])]})])],"derivedFrom":makeQuery(id+"F8.boolean.opBoolean","MERGE",FACE,{"derivedFrom":[makeQuery(id+"F6.boolean.opBoolean","COPY",FACE,{"derivedFrom":makeQuery(id+"F6.opExtrude","SWEPT_FACE",FACE,{"disambiguationData":[OSD([sQuery(id+"F5.wireOp",EDGE,"E27")])]})}),makeQuery(id+"F8.opExtrude","SWEPT_FACE",FACE,{"disambiguationData":[OSD([sQuery(id+"F7.wireOp",EDGE,"E31")])]})]})});
            var sketch = newSketch(context, id + "F41", { "sketchPlane" : qUnion([Q0])});
            skLineSegment(sketch, "E139", {"start": v(285.64, 18921.75) * mm, "end": v(2545.02, 16764) * mm});
            skLineSegment(sketch, "E140", {"start": v(2545.02, 16764) * mm, "end": v(285.64, 16764) * mm});
            skLineSegment(sketch, "E141", {"start": v(285.64, 16764) * mm, "end": v(285.64, 18921.75) * mm});
            skSolve(sketch);
        }
        {
            var Q0;
            Q0=qSketchRegion(id+"F41",true);
            extrude(context, id + "F42", {"entities" : qUnion([Q0]), "operationType" : NewBodyOperationType.ADD, "depth" : 127 * mm});
        }
        {
            var Q0;
            Q0=makeQuery(id+"F22.boolean.opBoolean","SPLIT",FACE,{"disambiguationData":[TD([makeQuery(id+"F2.opExtrude","SWEPT_FACE",FACE,{"disambiguationData":[OSD([sQuery(id+"F1.wireOp",EDGE,"E3")])]})])],"derivedFrom":makeQuery(id+"F4.boolean.opBoolean","COPY",FACE,{"derivedFrom":makeQuery(id+"F4.opExtrude","SWEPT_FACE",FACE,{"disambiguationData":[OSD([sQuery(id+"F3.wireOp",EDGE,"E16")])]})})});
            var sketch = newSketch(context, id + "F43", { "sketchPlane" : qUnion([Q0])});
            skLineSegment(sketch, "E142", {"start": v(5431.9, 15857.54) * mm, "end": v(3503.46, 13083.85) * mm});
            skLineSegment(sketch, "E143", {"start": v(3503.46, 13083.85) * mm, "end": v(3642.91, 12986.9) * mm});
            skLineSegment(sketch, "E144", {"start": v(3642.91, 12986.9) * mm, "end": v(5571.35, 15760.59) * mm});
            skLineSegment(sketch, "E145", {"start": v(5571.35, 15760.59) * mm, "end": v(5431.9, 15857.54) * mm});
            skLineSegment(sketch, "E146", {"start": v(2743.2, 13324.2) * mm, "end": v(2743.2, 15864.2) * mm, "construction": true});
            skLineSegment(sketch, "E147.MirrorCS", {"start": v(-84.95, 15760.59) * mm, "end": v(54.5, 15857.54) * mm});
            skLineSegment(sketch, "E148.MirrorCS", {"start": v(1982.94, 13083.85) * mm, "end": v(1843.49, 12986.9) * mm});
            skLineSegment(sketch, "E149.MirrorCS", {"start": v(54.5, 15857.54) * mm, "end": v(1982.94, 13083.85) * mm});
            skLineSegment(sketch, "E150.MirrorCS", {"start": v(1843.49, 12986.9) * mm, "end": v(-84.95, 15760.59) * mm});
            skSolve(sketch);
        }
        {
            var Q0;
            Q0=qSketchRegion(id+"F43",true);
            extrude(context, id + "F44", {"entities" : qUnion([Q0]), "operationType" : NewBodyOperationType.REMOVE, "endBound" : BoundingType.UP_TO_NEXT, "depth" : 25.4 * mm});
        }
        {
            var Q0;
            Q0=makeQuery(id+"F22.boolean.opBoolean","COPY",FACE,{"derivedFrom":makeQuery(id+"F22.opExtrude","SWEPT_FACE",FACE,{"disambiguationData":[OSD([sQuery(id+"F21.wireOp",EDGE,"E98")])]})});
            var sketch = newSketch(context, id + "F45", { "sketchPlane" : qUnion([Q0])});
            skLineSegment(sketch, "E151", {"start": v(-3822.7, 2946.4) * mm, "end": v(-3822.7, 203.2) * mm, "construction": true});
            skLineSegment(sketch, "E152.bottom", {"start": v(-4533.9, 2032) * mm, "end": v(-3111.5, 2032) * mm});
            skLineSegment(sketch, "E152.top", {"start": v(-4533.9, 863.6) * mm, "end": v(-3111.5, 863.6) * mm});
            skLineSegment(sketch, "E152.left", {"start": v(-4533.9, 2032) * mm, "end": v(-4533.9, 863.6) * mm});
            skLineSegment(sketch, "E152.right", {"start": v(-3111.5, 2032) * mm, "end": v(-3111.5, 863.6) * mm});
            skSolve(sketch);
        }
        {
            var Q0;
            Q0=qSketchRegion(id+"F45",true);
            extrude(context, id + "F46", {"entities" : qUnion([Q0]), "operationType" : NewBodyOperationType.REMOVE, "endBound" : BoundingType.UP_TO_NEXT, "oppositeDirection" : true, "depth" : 25.4 * mm});
        }
        {
            var Q0;
            Q0=makeQuery(id+"F22.boolean.opBoolean","COPY",FACE,{"derivedFrom":makeQuery(id+"F22.opExtrude","SWEPT_FACE",FACE,{"disambiguationData":[OSD([sQuery(id+"F21.wireOp",EDGE,"E83")])]})});
            var sketch = newSketch(context, id + "F47", { "sketchPlane" : qUnion([Q0])});
            skLineSegment(sketch, "E153", {"start": v(3048, 2946.4) * mm, "end": v(3048, 203.2) * mm, "construction": true});
            skLineSegment(sketch, "E154.bottom", {"start": v(2336.8, 2032) * mm, "end": v(3759.2, 2032) * mm});
            skLineSegment(sketch, "E154.top", {"start": v(2336.8, 863.6) * mm, "end": v(3759.2, 863.6) * mm});
            skLineSegment(sketch, "E154.left", {"start": v(2336.8, 2032) * mm, "end": v(2336.8, 863.6) * mm});
            skLineSegment(sketch, "E154.right", {"start": v(3759.2, 2032) * mm, "end": v(3759.2, 863.6) * mm});
            skSolve(sketch);
        }
        {
            var Q0;
            Q0=qSketchRegion(id+"F47",true);
            extrude(context, id + "F48", {"entities" : qUnion([Q0]), "operationType" : NewBodyOperationType.REMOVE, "endBound" : BoundingType.UP_TO_NEXT, "oppositeDirection" : true, "depth" : 25.4 * mm});
        }
        {
            var Q0;
            Q0=makeQuery(id+"F22.boolean.opBoolean","COPY",FACE,{"derivedFrom":makeQuery(id+"F22.opExtrude","SWEPT_FACE",FACE,{"disambiguationData":[OSD([sQuery(id+"F21.wireOp",EDGE,"E85")])]})});
            var sketch = newSketch(context, id + "F49", { "sketchPlane" : qUnion([Q0])});
            skLineSegment(sketch, "E155", {"start": v(-3048, 2946.4) * mm, "end": v(-3048, 203.2) * mm, "construction": true});
            skLineSegment(sketch, "E156.bottom", {"start": v(-3759.2, 2032) * mm, "end": v(-2336.8, 2032) * mm});
            skLineSegment(sketch, "E156.top", {"start": v(-3759.2, 863.6) * mm, "end": v(-2336.8, 863.6) * mm});
            skLineSegment(sketch, "E156.left", {"start": v(-3759.2, 2032) * mm, "end": v(-3759.2, 863.6) * mm});
            skLineSegment(sketch, "E156.right", {"start": v(-2336.8, 2032) * mm, "end": v(-2336.8, 863.6) * mm});
            skSolve(sketch);
        }
        {
            var Q0;
            Q0=qSketchRegion(id+"F49",true);
            extrude(context, id + "F50", {"entities" : qUnion([Q0]), "operationType" : NewBodyOperationType.REMOVE, "endBound" : BoundingType.UP_TO_NEXT, "oppositeDirection" : true, "depth" : 25.4 * mm});
        }
        {
            var Q0;
            Q0=makeQuery(id+"F22.boolean.opBoolean","COPY",FACE,{"derivedFrom":makeQuery(id+"F22.opExtrude","SWEPT_FACE",FACE,{"disambiguationData":[OSD([sQuery(id+"F21.wireOp",EDGE,"E77.left")])]})});
            var sketch = newSketch(context, id + "F51", { "sketchPlane" : qUnion([Q0])});
            skLineSegment(sketch, "E157", {"start": v(8318.5, 2946.4) * mm, "end": v(8318.5, 203.2) * mm, "construction": true});
            skLineSegment(sketch, "E158.bottom", {"start": v(7607.3, 2159) * mm, "end": v(9029.7, 2159) * mm});
            skLineSegment(sketch, "E158.top", {"start": v(7607.3, 1244.6) * mm, "end": v(9029.7, 1244.6) * mm});
            skLineSegment(sketch, "E158.left", {"start": v(7607.3, 2159) * mm, "end": v(7607.3, 1244.6) * mm});
            skLineSegment(sketch, "E158.right", {"start": v(9029.7, 2159) * mm, "end": v(9029.7, 1244.6) * mm});
            skSolve(sketch);
        }
        {
            var Q0;
            Q0=qSketchRegion(id+"F51",true);
            extrude(context, id + "F52", {"entities" : qUnion([Q0]), "operationType" : NewBodyOperationType.REMOVE, "endBound" : BoundingType.UP_TO_NEXT, "oppositeDirection" : true, "depth" : 25.4 * mm});
        }
        {
            var Q0;
            Q0=makeQuery(id+"F22.boolean.opBoolean","COPY",FACE,{"derivedFrom":makeQuery(id+"F22.opExtrude","SWEPT_FACE",FACE,{"disambiguationData":[OSD([sQuery(id+"F21.wireOp",EDGE,"E93")])]})});
            var sketch = newSketch(context, id + "F53", { "sketchPlane" : qUnion([Q0])});
            skLineSegment(sketch, "E159", {"start": v(-8318.5, 2946.4) * mm, "end": v(-8318.5, 203.2) * mm, "construction": true});
            skLineSegment(sketch, "E160.bottom", {"start": v(-9029.7, 2032) * mm, "end": v(-7607.3, 2032) * mm});
            skLineSegment(sketch, "E160.top", {"start": v(-9029.7, 1016) * mm, "end": v(-7607.3, 1016) * mm});
            skLineSegment(sketch, "E160.left", {"start": v(-9029.7, 2032) * mm, "end": v(-9029.7, 1016) * mm});
            skLineSegment(sketch, "E160.right", {"start": v(-7607.3, 2032) * mm, "end": v(-7607.3, 1016) * mm});
            skSolve(sketch);
        }
        {
            var Q0;
            Q0=qSketchRegion(id+"F53",true);
            extrude(context, id + "F54", {"entities" : qUnion([Q0]), "operationType" : NewBodyOperationType.REMOVE, "endBound" : BoundingType.UP_TO_NEXT, "oppositeDirection" : true, "depth" : 25.4 * mm});
        }
        {
            var Q0;
            Q0=makeQuery(id+"F22.boolean.opBoolean","COPY",FACE,{"derivedFrom":makeQuery(id+"F22.opExtrude","SWEPT_FACE",FACE,{"disambiguationData":[OSD([sQuery(id+"F21.wireOp",EDGE,"E73.left")])]})});
            var sketch = newSketch(context, id + "F55", { "sketchPlane" : qUnion([Q0])});
            skLineSegment(sketch, "E161", {"start": v(14808.2, 2946.4) * mm, "end": v(14808.2, 203.2) * mm, "construction": true});
            skLineSegment(sketch, "E162.bottom", {"start": v(14097, 2032) * mm, "end": v(15519.4, 2032) * mm});
            skLineSegment(sketch, "E162.top", {"start": v(14097, 863.6) * mm, "end": v(15519.4, 863.6) * mm});
            skLineSegment(sketch, "E162.left", {"start": v(14097, 2032) * mm, "end": v(14097, 863.6) * mm});
            skLineSegment(sketch, "E162.right", {"start": v(15519.4, 2032) * mm, "end": v(15519.4, 863.6) * mm});
            skSolve(sketch);
        }
        {
            var Q0;
            Q0=qSketchRegion(id+"F55",true);
            extrude(context, id + "F56", {"entities" : qUnion([Q0]), "operationType" : NewBodyOperationType.REMOVE, "endBound" : BoundingType.UP_TO_NEXT, "oppositeDirection" : true, "depth" : 25.4 * mm});
        }
        {
            var Q0;
            Q0=makeQuery(id+"F22.boolean.opBoolean","COPY",FACE,{"derivedFrom":makeQuery(id+"F22.opExtrude","SWEPT_FACE",FACE,{"disambiguationData":[OSD([sQuery(id+"F21.wireOp",EDGE,"E70.right")])]})});
            var sketch = newSketch(context, id + "F57", { "sketchPlane" : qUnion([Q0])});
            skLineSegment(sketch, "E163", {"start": v(-14808.2, 2946.4) * mm, "end": v(-14808.2, 203.2) * mm, "construction": true});
            skLineSegment(sketch, "E164.bottom", {"start": v(-15519.4, 2032) * mm, "end": v(-14097, 2032) * mm});
            skLineSegment(sketch, "E164.top", {"start": v(-15519.4, 863.6) * mm, "end": v(-14097, 863.6) * mm});
            skLineSegment(sketch, "E164.left", {"start": v(-15519.4, 2032) * mm, "end": v(-15519.4, 863.6) * mm});
            skLineSegment(sketch, "E164.right", {"start": v(-14097, 2032) * mm, "end": v(-14097, 863.6) * mm});
            skSolve(sketch);
        }
        {
            var Q0;
            Q0=qSketchRegion(id+"F57",true);
            extrude(context, id + "F58", {"entities" : qUnion([Q0]), "operationType" : NewBodyOperationType.REMOVE, "endBound" : BoundingType.UP_TO_NEXT, "oppositeDirection" : true, "depth" : 25.4 * mm});
        }
        {
            var Q0;
            Q0=makeQuery(id+"F22.boolean.opBoolean","COPY",FACE,{"derivedFrom":makeQuery(id+"F22.opExtrude","SWEPT_FACE",FACE,{"disambiguationData":[OSD([sQuery(id+"F21.wireOp",EDGE,"E90")])]})});
            var sketch = newSketch(context, id + "F59", { "sketchPlane" : qUnion([Q0])});
            skLineSegment(sketch, "E165.bottom", {"start": v(3962.4, 203.2) * mm, "end": v(3200.4, 203.2) * mm});
            skLineSegment(sketch, "E165.top", {"start": v(3962.4, 2336.8) * mm, "end": v(3200.4, 2336.8) * mm});
            skLineSegment(sketch, "E165.left", {"start": v(3962.4, 203.2) * mm, "end": v(3962.4, 2336.8) * mm});
            skLineSegment(sketch, "E165.right", {"start": v(3200.4, 203.2) * mm, "end": v(3200.4, 2336.8) * mm});
            skSolve(sketch);
        }
        {
            var Q0;
            Q0=qSketchRegion(id+"F59",true);
            extrude(context, id + "F60", {"entities" : qUnion([Q0]), "operationType" : NewBodyOperationType.REMOVE, "endBound" : BoundingType.UP_TO_NEXT, "oppositeDirection" : true, "depth" : 25.4 * mm});
        }
        {
            var Q0;
            Q0=makeQuery(id+"F22.boolean.opBoolean","COPY",FACE,{"derivedFrom":makeQuery(id+"F22.opExtrude","SWEPT_FACE",FACE,{"disambiguationData":[OSD([sQuery(id+"F21.wireOp",EDGE,"E88")])]})});
            var sketch = newSketch(context, id + "F61", { "sketchPlane" : qUnion([Q0])});
            skLineSegment(sketch, "E166.bottom", {"start": v(4419.6, 203.2) * mm, "end": v(5181.6, 203.2) * mm});
            skLineSegment(sketch, "E166.top", {"start": v(4419.6, 2235.2) * mm, "end": v(5181.6, 2235.2) * mm});
            skLineSegment(sketch, "E166.left", {"start": v(4419.6, 203.2) * mm, "end": v(4419.6, 2235.2) * mm});
            skLineSegment(sketch, "E166.right", {"start": v(5181.6, 203.2) * mm, "end": v(5181.6, 2235.2) * mm});
            skSolve(sketch);
        }
        {
            var Q0;
            Q0=qSketchRegion(id+"F61",true);
            extrude(context, id + "F62", {"entities" : qUnion([Q0]), "operationType" : NewBodyOperationType.REMOVE, "endBound" : BoundingType.UP_TO_NEXT, "oppositeDirection" : true, "depth" : 25.4 * mm});
        }
        {
            var Q0;
            Q0=makeQuery(id+"F22.boolean.opBoolean","COPY",FACE,{"derivedFrom":makeQuery(id+"F22.opExtrude","SWEPT_FACE",FACE,{"disambiguationData":[OSD([sQuery(id+"F21.wireOp",EDGE,"E101")])]})});
            var sketch = newSketch(context, id + "F63", { "sketchPlane" : qUnion([Q0])});
            skLineSegment(sketch, "E167", {"start": v(6553.2, 203.2) * mm, "end": v(4419.6, 203.2) * mm});
            skLineSegment(sketch, "E168", {"start": v(4419.6, 203.2) * mm, "end": v(4419.6, 2605.79) * mm});
            skLineSegment(sketch, "E169", {"start": v(4419.6, 2605.79) * mm, "end": v(6553.2, 1957.6) * mm});
            skLineSegment(sketch, "E170", {"start": v(6553.2, 1957.6) * mm, "end": v(6553.2, 203.2) * mm});
            skSolve(sketch);
        }
        {
            var Q0;
            Q0=qSketchRegion(id+"F63",true);
            extrude(context, id + "F64", {"entities" : qUnion([Q0]), "operationType" : NewBodyOperationType.REMOVE, "endBound" : BoundingType.UP_TO_NEXT, "oppositeDirection" : true, "depth" : 25.4 * mm});
        }
        {
            var Q0;
            Q0=makeQuery(id+"F22.boolean.opBoolean","COPY",FACE,{"derivedFrom":makeQuery(id+"F22.opExtrude","SWEPT_FACE",FACE,{"disambiguationData":[OSD([sQuery(id+"F21.wireOp",EDGE,"E77.right")])]})});
            var sketch = newSketch(context, id + "F65", { "sketchPlane" : qUnion([Q0])});
            skLineSegment(sketch, "E171", {"start": v(-8318.5, 2946.4) * mm, "end": v(-8318.5, 203.2) * mm, "construction": true});
            skLineSegment(sketch, "E172.bottom", {"start": v(-8699.5, 203.2) * mm, "end": v(-7937.5, 203.2) * mm});
            skLineSegment(sketch, "E172.top", {"start": v(-8699.5, 2336.8) * mm, "end": v(-7937.5, 2336.8) * mm});
            skLineSegment(sketch, "E172.left", {"start": v(-8699.5, 203.2) * mm, "end": v(-8699.5, 2336.8) * mm});
            skLineSegment(sketch, "E172.right", {"start": v(-7937.5, 203.2) * mm, "end": v(-7937.5, 2336.8) * mm});
            skSolve(sketch);
        }
        {
            var Q0;
            Q0=qSketchRegion(id+"F65",true);
            extrude(context, id + "F66", {"entities" : qUnion([Q0]), "operationType" : NewBodyOperationType.REMOVE, "endBound" : BoundingType.UP_TO_NEXT, "oppositeDirection" : true, "depth" : 25.4 * mm});
        }
        {
            var Q0;
            Q0=makeQuery(id+"F22.boolean.opBoolean","COPY",FACE,{"derivedFrom":makeQuery(id+"F22.opExtrude","SWEPT_FACE",FACE,{"disambiguationData":[OSD([sQuery(id+"F21.wireOp",EDGE,"E77.bottom")])]})});
            var sketch = newSketch(context, id + "F67", { "sketchPlane" : qUnion([Q0])});
            skLineSegment(sketch, "E173.bottom", {"start": v(3200.4, 203.2) * mm, "end": v(3962.4, 203.2) * mm});
            skLineSegment(sketch, "E173.top", {"start": v(3200.4, 2336.8) * mm, "end": v(3962.4, 2336.8) * mm});
            skLineSegment(sketch, "E173.left", {"start": v(3200.4, 203.2) * mm, "end": v(3200.4, 2336.8) * mm});
            skLineSegment(sketch, "E173.right", {"start": v(3962.4, 203.2) * mm, "end": v(3962.4, 2336.8) * mm});
            skSolve(sketch);
        }
        {
            var Q0;
            Q0=qSketchRegion(id+"F67",true);
            extrude(context, id + "F68", {"entities" : qUnion([Q0]), "operationType" : NewBodyOperationType.REMOVE, "endBound" : BoundingType.UP_TO_NEXT, "oppositeDirection" : true, "depth" : 25.4 * mm});
        }
        {
            var Q0;
            Q0=makeQuery(id+"F28.boolean.opBoolean","MERGE",FACE,{"derivedFrom":[makeQuery(id+"F22.boolean.opBoolean","MERGE",FACE,{"derivedFrom":[makeQuery(id+"F16.boolean.opBoolean","MERGE",FACE,{"derivedFrom":[makeQuery(id+"F14.boolean.opBoolean","MERGE",FACE,{"derivedFrom":[makeQuery(id+"F12.boolean.opBoolean","MERGE",FACE,{"derivedFrom":[makeQuery(id+"F2.opExtrude","SWEPT_FACE",FACE,{"disambiguationData":[OSD([sQuery(id+"F1.wireOp",EDGE,"E3")])]}),makeQuery(id+"F12.opExtrude","SWEPT_FACE",FACE,{"disambiguationData":[OSD([sQuery(id+"F11.wireOp",EDGE,"E43")])]})]}),makeQuery(id+"F14.opExtrude","SWEPT_FACE",FACE,{"disambiguationData":[OSD([sQuery(id+"F13.wireOp",EDGE,"E48")])]})]}),makeQuery(id+"F16.opExtrude","CAP_FACE",FACE,{"disambiguationData":[OSD([sQuery(id+"F15.wireOp",EDGE,"E53"),sQuery(id+"F15.wireOp",EDGE,"E54.MirrorCS"),sQuery(id+"F15.wireOp",EDGE,"E55")])],"isStart":true})]}),makeQuery(id+"F22.opExtrude","SWEPT_FACE",FACE,{"disambiguationData":[OSD([sQuery(id+"F21.wireOp",EDGE,"E70.left")])]}),makeQuery(id+"F22.opExtrude","SWEPT_FACE",FACE,{"disambiguationData":[OSD([sQuery(id+"F21.wireOp",EDGE,"E71.left")])]}),makeQuery(id+"F22.opExtrude","SWEPT_FACE",FACE,{"disambiguationData":[OSD([sQuery(id+"F21.wireOp",EDGE,"E82.left")])]})]}),makeQuery(id+"F28.opExtrude","SWEPT_FACE",FACE,{"disambiguationData":[OSD([sQuery(id+"F27.wireOp",EDGE,"E118")])]})]});
            var sketch = newSketch(context, id + "F69", { "sketchPlane" : qUnion([Q0])});
            skLineSegment(sketch, "E174.bottom", {"start": v(15189.2, 203.2) * mm, "end": v(15951.2, 203.2) * mm});
            skLineSegment(sketch, "E174.top", {"start": v(15189.2, 2032) * mm, "end": v(15951.2, 2032) * mm});
            skLineSegment(sketch, "E174.left", {"start": v(15189.2, 203.2) * mm, "end": v(15189.2, 2032) * mm});
            skLineSegment(sketch, "E174.right", {"start": v(15951.2, 203.2) * mm, "end": v(15951.2, 2032) * mm});
            skLineSegment(sketch, "E175.bottom", {"start": v(14909.8, 203.2) * mm, "end": v(14147.8, 203.2) * mm});
            skLineSegment(sketch, "E175.top", {"start": v(14909.8, 2336.8) * mm, "end": v(14147.8, 2336.8) * mm});
            skLineSegment(sketch, "E175.left", {"start": v(14909.8, 203.2) * mm, "end": v(14909.8, 2336.8) * mm});
            skLineSegment(sketch, "E175.right", {"start": v(14147.8, 203.2) * mm, "end": v(14147.8, 2336.8) * mm});
            skSolve(sketch);
        }
        {
            var Q0;
            Q0=qSketchRegion(id+"F69",true);
            extrude(context, id + "F70", {"entities" : qUnion([Q0]), "operationType" : NewBodyOperationType.REMOVE, "endBound" : BoundingType.UP_TO_NEXT, "oppositeDirection" : true, "depth" : 25.4 * mm});
        }
        {
            var Q0;
            Q0=makeQuery(id+"F38.boolean.opBoolean","MERGE",FACE,{"derivedFrom":[makeQuery(id+"F34.boolean.opBoolean","MERGE",FACE,{"derivedFrom":[makeQuery(id+"F22.boolean.opBoolean","COPY",FACE,{"derivedFrom":makeQuery(id+"F22.opExtrude","SWEPT_FACE",FACE,{"disambiguationData":[OSD([sQuery(id+"F21.wireOp",EDGE,"E91")])]})}),makeQuery(id+"F34.opExtrude","SWEPT_FACE",FACE,{"disambiguationData":[OSD([sQuery(id+"F33.wireOp",EDGE,"E126.left")])]})]}),makeQuery(id+"F38.opExtrude","CAP_FACE",FACE,{"disambiguationData":[OSD([sQuery(id+"F37.wireOp",EDGE,"E133"),sQuery(id+"F37.wireOp",EDGE,"E134"),sQuery(id+"F37.wireOp",EDGE,"E135")])],"isStart":true})]});
            var sketch = newSketch(context, id + "F71", { "sketchPlane" : qUnion([Q0])});
            skLineSegment(sketch, "E176.bottom", {"start": v(14528.8, 203.2) * mm, "end": v(15290.8, 203.2) * mm});
            skLineSegment(sketch, "E176.top", {"start": v(14528.8, 2336.8) * mm, "end": v(15290.8, 2336.8) * mm});
            skLineSegment(sketch, "E176.left", {"start": v(14528.8, 203.2) * mm, "end": v(14528.8, 2336.8) * mm});
            skLineSegment(sketch, "E176.right", {"start": v(15290.8, 203.2) * mm, "end": v(15290.8, 2336.8) * mm});
            skSolve(sketch);
        }
        {
            var Q0;
            Q0=qSketchRegion(id+"F71",true);
            extrude(context, id + "F72", {"entities" : qUnion([Q0]), "operationType" : NewBodyOperationType.REMOVE, "endBound" : BoundingType.UP_TO_NEXT, "oppositeDirection" : true, "depth" : 25.4 * mm});
        }
        {
            var Q0;
            Q0=makeQuery(id+"F22.boolean.opBoolean","COPY",FACE,{"derivedFrom":makeQuery(id+"F22.opExtrude","SWEPT_FACE",FACE,{"disambiguationData":[OSD([sQuery(id+"F21.wireOp",EDGE,"E73.top")])]})});
            var sketch = newSketch(context, id + "F73", { "sketchPlane" : qUnion([Q0])});
            skLineSegment(sketch, "E177.bottom", {"start": v(-4064, 203.2) * mm, "end": v(-3302, 203.2) * mm});
            skLineSegment(sketch, "E177.top", {"start": v(-4064, 2336.8) * mm, "end": v(-3302, 2336.8) * mm});
            skLineSegment(sketch, "E177.left", {"start": v(-4064, 203.2) * mm, "end": v(-4064, 2336.8) * mm});
            skLineSegment(sketch, "E177.right", {"start": v(-3302, 203.2) * mm, "end": v(-3302, 2336.8) * mm});
            skSolve(sketch);
        }
        {
            var Q0;
            Q0=qSketchRegion(id+"F73",true);
            extrude(context, id + "F74", {"entities" : qUnion([Q0]), "operationType" : NewBodyOperationType.REMOVE, "endBound" : BoundingType.UP_TO_NEXT, "oppositeDirection" : true, "depth" : 25.4 * mm});
        }
        {
            var Q0;
            Q0=makeQuery(id+"F74.boolean.opBoolean","MERGE",FACE,{"derivedFrom":[makeQuery(id+"F22.boolean.opBoolean","COPY",FACE,{"derivedFrom":makeQuery(id+"F22.opExtrude","CAP_FACE",FACE,{"disambiguationData":[OSD([sQuery(id+"F21.wireOp",EDGE,"E75.bottom"),sQuery(id+"F21.wireOp",EDGE,"E75.top"),sQuery(id+"F21.wireOp",EDGE,"E75.left"),sQuery(id+"F21.wireOp",EDGE,"E75.right")])],"isStart":false})}),makeQuery(id+"F72.boolean.opBoolean","MERGE",FACE,{"derivedFrom":[makeQuery(id+"F22.boolean.opBoolean","COPY",FACE,{"derivedFrom":makeQuery(id+"F22.opExtrude","CAP_FACE",FACE,{"disambiguationData":[OSD([sQuery(id+"F21.wireOp",EDGE,"E73.bottom"),sQuery(id+"F21.wireOp",EDGE,"E73.top"),sQuery(id+"F21.wireOp",EDGE,"E73.left"),sQuery(id+"F21.wireOp",EDGE,"E73.right")])],"isStart":false})}),makeQuery(id+"F70.boolean.opBoolean","MERGE",FACE,{"derivedFrom":[makeQuery(id+"F22.boolean.opBoolean","COPY",FACE,{"derivedFrom":makeQuery(id+"F22.opExtrude","CAP_FACE",FACE,{"disambiguationData":[OSD([sQuery(id+"F21.wireOp",EDGE,"E70.bottom"),sQuery(id+"F21.wireOp",EDGE,"E70.top"),sQuery(id+"F21.wireOp",EDGE,"E70.left"),sQuery(id+"F21.wireOp",EDGE,"E70.right")])],"isStart":false})}),makeQuery(id+"F22.boolean.opBoolean","COPY",FACE,{"derivedFrom":makeQuery(id+"F22.opExtrude","CAP_FACE",FACE,{"disambiguationData":[OSD([sQuery(id+"F21.wireOp",EDGE,"E72.bottom"),sQuery(id+"F21.wireOp",EDGE,"E72.top"),sQuery(id+"F21.wireOp",EDGE,"E72.left"),sQuery(id+"F21.wireOp",EDGE,"E72.right")])],"isStart":false})}),makeQuery(id+"F68.boolean.opBoolean","MERGE",FACE,{"derivedFrom":[makeQuery(id+"F22.boolean.opBoolean","COPY",FACE,{"derivedFrom":makeQuery(id+"F22.opExtrude","CAP_FACE",FACE,{"disambiguationData":[OSD([sQuery(id+"F21.wireOp",EDGE,"E76.bottom"),sQuery(id+"F21.wireOp",EDGE,"E76.top"),sQuery(id+"F21.wireOp",EDGE,"E76.left"),sQuery(id+"F21.wireOp",EDGE,"E76.right")])],"isStart":false})}),makeQuery(id+"F66.boolean.opBoolean","MERGE",FACE,{"derivedFrom":[makeQuery(id+"F22.boolean.opBoolean","COPY",FACE,{"derivedFrom":makeQuery(id+"F22.opExtrude","CAP_FACE",FACE,{"disambiguationData":[OSD([sQuery(id+"F21.wireOp",EDGE,"E77.bottom"),sQuery(id+"F21.wireOp",EDGE,"E77.top"),sQuery(id+"F21.wireOp",EDGE,"E77.left"),sQuery(id+"F21.wireOp",EDGE,"E77.right")])],"isStart":false})}),makeQuery(id+"F64.boolean.opBoolean","MERGE",FACE,{"derivedFrom":[makeQuery(id+"F22.boolean.opBoolean","COPY",FACE,{"derivedFrom":makeQuery(id+"F22.opExtrude","CAP_FACE",FACE,{"disambiguationData":[OSD([sQuery(id+"F21.wireOp",EDGE,"E91"),sQuery(id+"F21.wireOp",EDGE,"E94"),sQuery(id+"F21.wireOp",EDGE,"E95"),sQuery(id+"F21.wireOp",EDGE,"E96"),sQuery(id+"F21.wireOp",EDGE,"E102"),sQuery(id+"F21.wireOp",EDGE,"E104.trimOffspring")])],"isStart":false})}),makeQuery(id+"F62.boolean.opBoolean","MERGE",FACE,{"derivedFrom":[makeQuery(id+"F22.boolean.opBoolean","COPY",FACE,{"derivedFrom":makeQuery(id+"F22.opExtrude","CAP_FACE",FACE,{"disambiguationData":[OSD([sQuery(id+"F21.wireOp",EDGE,"E92"),sQuery(id+"F21.wireOp",EDGE,"E93"),sQuery(id+"F21.wireOp",EDGE,"E101"),sQuery(id+"F21.wireOp",EDGE,"E103.trimOffspring")])],"isStart":false})}),makeQuery(id+"F60.boolean.opBoolean","MERGE",FACE,{"derivedFrom":[makeQuery(id+"F22.boolean.opBoolean","COPY",FACE,{"derivedFrom":makeQuery(id+"F22.opExtrude","CAP_FACE",FACE,{"disambiguationData":[OSD([sQuery(id+"F21.wireOp",EDGE,"E79.bottom"),sQuery(id+"F21.wireOp",EDGE,"E79.top"),sQuery(id+"F21.wireOp",EDGE,"E79.left"),sQuery(id+"F21.wireOp",EDGE,"E79.right")])],"isStart":false})}),makeQuery(id+"F22.boolean.opBoolean","COPY",FACE,{"derivedFrom":makeQuery(id+"F22.opExtrude","CAP_FACE",FACE,{"disambiguationData":[OSD([sQuery(id+"F21.wireOp",EDGE,"E83"),sQuery(id+"F21.wireOp",EDGE,"E84"),sQuery(id+"F21.wireOp",EDGE,"E85"),sQuery(id+"F21.wireOp",EDGE,"E86"),sQuery(id+"F21.wireOp",EDGE,"E87"),sQuery(id+"F21.wireOp",EDGE,"E88"),sQuery(id+"F21.wireOp",EDGE,"E89"),sQuery(id+"F21.wireOp",EDGE,"E90"),sQuery(id+"F21.wireOp",EDGE,"E97"),sQuery(id+"F21.wireOp",EDGE,"E98"),sQuery(id+"F21.wireOp",EDGE,"E99"),sQuery(id+"F21.wireOp",EDGE,"E100.trimOffspring")])],"isStart":false})}),makeQuery(id+"F60.opExtrude","SWEPT_FACE",FACE,{"disambiguationData":[OSD([sQuery(id+"F59.wireOp",EDGE,"E165.bottom")])]})]}),makeQuery(id+"F62.opExtrude","SWEPT_FACE",FACE,{"disambiguationData":[OSD([sQuery(id+"F61.wireOp",EDGE,"E166.bottom")])]})]}),makeQuery(id+"F64.opExtrude","SWEPT_FACE",FACE,{"disambiguationData":[OSD([sQuery(id+"F63.wireOp",EDGE,"E167")])]})]}),makeQuery(id+"F66.opExtrude","SWEPT_FACE",FACE,{"disambiguationData":[OSD([sQuery(id+"F65.wireOp",EDGE,"E172.bottom")])]})]}),makeQuery(id+"F68.opExtrude","SWEPT_FACE",FACE,{"disambiguationData":[OSD([sQuery(id+"F67.wireOp",EDGE,"E173.bottom")])]})]}),makeQuery(id+"F70.opExtrude","SWEPT_FACE",FACE,{"disambiguationData":[OSD([sQuery(id+"F69.wireOp",EDGE,"E174.bottom")])]}),makeQuery(id+"F70.opExtrude","SWEPT_FACE",FACE,{"disambiguationData":[OSD([sQuery(id+"F69.wireOp",EDGE,"E175.bottom")])]})]}),makeQuery(id+"F72.opExtrude","SWEPT_FACE",FACE,{"disambiguationData":[OSD([sQuery(id+"F71.wireOp",EDGE,"E176.bottom")])]})]}),makeQuery(id+"F74.opExtrude","SWEPT_FACE",FACE,{"disambiguationData":[OSD([sQuery(id+"F73.wireOp",EDGE,"E177.bottom")])]})]});
            var sketch = newSketch(context, id + "F75", { "sketchPlane" : qUnion([Q0])});
            skLineSegment(sketch, "E178", {"start": v(127, 9080.5) * mm, "end": v(736.6, 9080.5) * mm});
            skLineSegment(sketch, "E179", {"start": v(736.6, 9080.5) * mm, "end": v(736.6, 7404.1) * mm});
            skLineSegment(sketch, "E180", {"start": v(736.6, 7404.1) * mm, "end": v(2616.2, 7404.1) * mm});
            skLineSegment(sketch, "E181", {"start": v(2616.2, 7404.1) * mm, "end": v(2616.2, 6794.5) * mm});
            skLineSegment(sketch, "E182", {"start": v(2616.2, 6794.5) * mm, "end": v(127, 6794.5) * mm});
            skLineSegment(sketch, "E183", {"start": v(127, 6794.5) * mm, "end": v(127, 9080.5) * mm});
            skSolve(sketch);
        }
        {
            var Q0;
            Q0=qSketchRegion(id+"F75",true);
            extrude(context, id + "F76", {"entities" : qUnion([Q0]), "operationType" : NewBodyOperationType.ADD, "depth" : 838.2 * mm});
        }
        {
            var Q0;
            Q0=makeQuery(id+"F76.opExtrude","CAP_FACE",FACE,{"disambiguationData":[OSD([sQuery(id+"F75.wireOp",EDGE,"E178"),sQuery(id+"F75.wireOp",EDGE,"E179"),sQuery(id+"F75.wireOp",EDGE,"E180"),sQuery(id+"F75.wireOp",EDGE,"E181"),sQuery(id+"F75.wireOp",EDGE,"E182"),sQuery(id+"F75.wireOp",EDGE,"E183")])],"isStart":false});
            var sketch = newSketch(context, id + "F77", { "sketchPlane" : qUnion([Q0])});
            skLineSegment(sketch, "E184", {"start": v(127, 8293.1) * mm, "end": v(736.6, 8293.1) * mm, "construction": true});
            skEllipse(sketch, "E185", {"center": v(431.8, 8293.1) * mm, "majorRadius": 228.6 * mm, "minorRadius": 177.8 * mm, "majorAxis": v(0, -1)});
            skSolve(sketch);
        }
        {
            var Q0;
            Q0=qSketchRegion(id+"F77",true);
            extrude(context, id + "F78", {"entities" : qUnion([Q0]), "operationType" : NewBodyOperationType.REMOVE, "oppositeDirection" : true, "depth" : 304.8 * mm});
        }
        {
            var Q0;
            Q0=makeQuery(id+"F2.opExtrude","CAP_FACE",FACE,{"disambiguationData":[OSD([sQuery(id+"F1.wireOp",EDGE,"E0"),sQuery(id+"F1.wireOp",EDGE,"E1"),sQuery(id+"F1.wireOp",EDGE,"E2"),sQuery(id+"F1.wireOp",EDGE,"E3"),sQuery(id+"F1.wireOp",EDGE,"E4"),sQuery(id+"F1.wireOp",EDGE,"E5"),sQuery(id+"F1.wireOp",EDGE,"E6"),sQuery(id+"F1.wireOp",EDGE,"E7"),sQuery(id+"F1.wireOp",EDGE,"E8"),sQuery(id+"F1.wireOp",EDGE,"E9")])],"isStart":true});
            var sketch = newSketch(context, id + "F79", { "sketchPlane" : qUnion([Q0])});
            skLineSegment(sketch, "E186", {"start": v(0, 0) * mm, "end": v(0, -482.6) * mm});
            skLineSegment(sketch, "E187", {"start": v(0, -482.6) * mm, "end": v(152.4, -482.6) * mm});
            skLineSegment(sketch, "E188", {"start": v(152.4, -482.6) * mm, "end": v(152.4, -152.4) * mm});
            skLineSegment(sketch, "E189", {"start": v(152.4, -152.4) * mm, "end": v(482.6, -152.4) * mm});
            skLineSegment(sketch, "E190", {"start": v(482.6, -152.4) * mm, "end": v(482.6, 0) * mm});
            skLineSegment(sketch, "E191", {"start": v(482.6, 0) * mm, "end": v(0, 0) * mm});
            skLineSegment(sketch, "E192", {"start": v(7645.4, 0) * mm, "end": v(7645.4, -482.6) * mm});
            skLineSegment(sketch, "E193", {"start": v(7645.4, -482.6) * mm, "end": v(7493, -482.6) * mm});
            skLineSegment(sketch, "E194", {"start": v(7493, -482.6) * mm, "end": v(7493, -152.4) * mm});
            skLineSegment(sketch, "E195", {"start": v(7493, -152.4) * mm, "end": v(7162.8, -152.4) * mm});
            skLineSegment(sketch, "E196", {"start": v(7162.8, -152.4) * mm, "end": v(7162.8, 0) * mm});
            skLineSegment(sketch, "E197", {"start": v(7162.8, 0) * mm, "end": v(7645.4, 0) * mm});
            skLineSegment(sketch, "E198", {"start": v(10363.2, -10541) * mm, "end": v(9880.6, -10541) * mm});
            skLineSegment(sketch, "E199", {"start": v(9880.6, -10541) * mm, "end": v(9880.6, -10693.4) * mm});
            skLineSegment(sketch, "E200", {"start": v(9880.6, -10693.4) * mm, "end": v(10210.8, -10693.4) * mm});
            skLineSegment(sketch, "E201", {"start": v(10210.8, -10693.4) * mm, "end": v(10210.8, -11023.6) * mm});
            skLineSegment(sketch, "E202", {"start": v(10210.8, -11023.6) * mm, "end": v(10363.2, -11023.6) * mm});
            skLineSegment(sketch, "E203", {"start": v(10363.2, -11023.6) * mm, "end": v(10363.2, -10541) * mm});
            skLineSegment(sketch, "E204", {"start": v(10363.2, -19075.4) * mm, "end": v(9880.6, -19075.4) * mm});
            skLineSegment(sketch, "E205", {"start": v(9880.6, -19075.4) * mm, "end": v(9880.6, -18923) * mm});
            skLineSegment(sketch, "E206", {"start": v(9880.6, -18923) * mm, "end": v(10210.8, -18923) * mm});
            skLineSegment(sketch, "E207", {"start": v(10210.8, -18923) * mm, "end": v(10210.8, -18592.8) * mm});
            skLineSegment(sketch, "E208", {"start": v(10210.8, -18592.8) * mm, "end": v(10363.2, -18592.8) * mm});
            skLineSegment(sketch, "E209", {"start": v(10363.2, -18592.8) * mm, "end": v(10363.2, -19075.4) * mm});
            skLineSegment(sketch, "E210", {"start": v(0, -23342.6) * mm, "end": v(0, -22860) * mm});
            skLineSegment(sketch, "E211", {"start": v(0, -22860) * mm, "end": v(152.4, -22860) * mm});
            skLineSegment(sketch, "E212", {"start": v(152.4, -22860) * mm, "end": v(152.4, -23190.2) * mm});
            skLineSegment(sketch, "E213", {"start": v(152.4, -23190.2) * mm, "end": v(482.6, -23190.2) * mm});
            skLineSegment(sketch, "E214", {"start": v(482.6, -23190.2) * mm, "end": v(482.6, -23342.6) * mm});
            skLineSegment(sketch, "E215", {"start": v(482.6, -23342.6) * mm, "end": v(0, -23342.6) * mm});
            skLineSegment(sketch, "E216", {"start": v(5486.4, -23342.6) * mm, "end": v(5486.4, -22860) * mm});
            skLineSegment(sketch, "E217", {"start": v(5486.4, -22860) * mm, "end": v(5334, -22860) * mm});
            skLineSegment(sketch, "E218", {"start": v(5334, -22860) * mm, "end": v(5334, -23190.2) * mm});
            skLineSegment(sketch, "E219", {"start": v(5334, -23190.2) * mm, "end": v(5003.8, -23190.2) * mm});
            skLineSegment(sketch, "E220", {"start": v(5003.8, -23190.2) * mm, "end": v(5003.8, -23342.6) * mm});
            skLineSegment(sketch, "E221", {"start": v(5003.8, -23342.6) * mm, "end": v(5486.4, -23342.6) * mm});
            skSolve(sketch);
        }
        {
            var Q0;
            Q0=qSketchRegion(id+"F79",true);
            extrude(context, id + "F80", {"entities" : qUnion([Q0]), "operationType" : NewBodyOperationType.REMOVE, "oppositeDirection" : true, "depth" : 127 * mm});
        }
    });
